FCSTD DOCUMENT  (FreeCAD 1.0R39109 (Git))
Label: bridge_S
License: All rights reserved
LicenseURL: https://en.wikipedia.org/wiki/All_rights_reserved
objects: Part::FeaturePython×26, Sketcher::SketchObject×11, Part::Extrusion×9, App::Part×5, Part::Sweep×4, Part::Compound×4, Part::MultiFuse×2, Spreadsheet::Sheet×1, Part::Mirroring×1, PartDesign::FeatureBase×1, PartDesign::Pocket×1, PartDesign::Body×1, Part::Feature×1, PartDesign::Pad×1
note: 74 computed .brp shape members not serialized (recipe doc carries the construction recipe); baked Part::Feature solids carry a one-line shape summary decoded from their .brp

FEATURE [Part::FeaturePython] HShapeSteel  # WARN: FeaturePython — macro-defined, semantics opaque (R4)
  B = 200
  H = 294
  L = 5500
  Placement = pos=(0,-500,0) rot=(0,0,1;1.5708rad)
  Solid = false
  g0 = 7.85
  mass = 0
  size = 3
  standard = SS_Medium
  t1 = 8
  t2 = 12
  type = 02_H_Shape
FEATURE [Spreadsheet::Sheet] Spreadsheet  label="Spreadsheet_bridge"
  cells = A2='tankDia; B2(dia)=13000; A3='bridgeLength; B3(L0)==dia + 600; A4='hight; B4(hight)=600
FEATURE [Part::Extrusion] Extrude
  Base = -> HShapeSteel
  Dir = (-1,-2e-16,0)
  DirMode = 2
  FaceMakerClass = Part::FaceMakerBullseye
  FaceMakerMode = 3
  LengthFwd = 13600
  LengthRev = 0
  Solid = false
  Symmetric = true
  expr: LengthFwd = Spreadsheet.L0
FEATURE [Part::FeaturePython] Clone  label="Extrude001"  # Draft clone (typed FeaturePython)
  AttacherType = Attacher::AttachEngine3D
  Fuse = false
  Objects = -> [Extrude]
  Placement = pos=(0,800,0) rot=(0,0,1;0rad)
  Scale = (1,1,1)
  expr: .Placement.Base.y = 1000 - HShapeSteel.B
FEATURE [Part::FeaturePython] ChannelSteel  # WARN: FeaturePython — macro-defined, semantics opaque (R4)
  B = 75
  H = 150
  L = 5500
  Placement = pos=(-1000,0,0) rot=(0,0,1;0rad)
  Solid = false
  g0 = 7.85
  mass = 0
  size = 3
  standard = SS
  t1 = 6.5
  t2 = 10
  type = 01_Channel
FEATURE [Sketcher::SketchObject] Sketch
  ArcFitTolerance = 1e-06
  FullyConstrained = true
  MakeInternals = false
  sketch-geometry (5):
    g0: LineSegment StartX=-1000 StartY=-1000 StartZ=0 EndX=1000 EndY=-1000 EndZ=0
    g1: LineSegment StartX=1000 StartY=-1000 StartZ=0 EndX=1000 EndY=1000 EndZ=0
    g2: LineSegment StartX=1000 StartY=1000 StartZ=0 EndX=-1000 EndY=1000 EndZ=0
    g3: LineSegment StartX=-1000 StartY=1000 StartZ=0 EndX=-1000 EndY=-1000 EndZ=0
    g4: GeomPoint [constr] X=0 Y=0 Z=0
  constraints (12):
    c: Coincident(g0,g1)
    c: Coincident(g1,g2)
    c: Coincident(g2,g3)
    c: Coincident(g3,g0)
    c: Horizontal(g0)
    c: Horizontal(g2)
    c: Vertical(g1)
    c: Vertical(g3)
    c: Symmetric(g2,g0,g4)
    c: Coincident(g4,g-1)
    c: DistanceX(g2,g2) = 2000
    c: DistanceY(g3,g3) = 2000
FEATURE [Part::Sweep] Sweep
  Frenet = true
  Placement = pos=(0,0,144) rot=(0,0,1;0rad)
  Sections = -> [ChannelSteel]
  Solid = true
  Spine = -> Sketch [Edge4,Edge3,Edge2,Edge1]
  Transition = 1
FEATURE [Part::FeaturePython] AngleSteel  # WARN: FeaturePython — macro-defined, semantics opaque (R4)
  A = 65
  B = 65
  L = 5500
  Placement = pos=(-6800,0,0) rot=(0,0,1;0rad)
  Solid = false
  g0 = 7.85
  mass = 0
  size = 8
  standard = SS_Equal
  t = 6
  type = 00_Angle
FEATURE [Part::FeaturePython] AngleSteel001  # WARN: FeaturePython — macro-defined, semantics opaque (R4)
  A = 65
  B = 65
  L = 5500
  Placement = pos=(-6800,0,294) rot=(0,1,0;1.5708rad)
  Solid = false
  g0 = 7.85
  mass = 0
  size = 8
  standard = SS_Equal
  t = 6
  type = 00_Angle
FEATURE [Part::Extrusion] Extrude001  label="Extrude002"
  Base = -> AngleSteel001
  Dir = (0,1,0)
  DirMode = 2
  FaceMakerClass = Part::FaceMakerBullseye
  FaceMakerMode = 3
  LengthFwd = 600
  LengthRev = 0
  Solid = false
  Symmetric = true
  expr: LengthFwd = 1000 - HShapeSteel.B * 2
FEATURE [Part::Extrusion] Extrude002  label="Extrude003"
  Base = -> AngleSteel
  Dir = (0,1,0)
  DirMode = 2
  FaceMakerClass = Part::FaceMakerBullseye
  FaceMakerMode = 3
  LengthFwd = 600
  LengthRev = 0
  Solid = false
  Symmetric = true
  expr: LengthFwd = 1000 - HShapeSteel.B * 2
FEATURE [Part::Compound] Compound
  Links = -> [Extrude001,Extrude002]
FEATURE [Part::FeaturePython] Array  # Draft array (typed FeaturePython)
  AlwaysSyncPlacement = false
  Angle = 360
  ArrayType = 0
  Axis = (0,0,1)
  Base = -> Compound
  Center = (0,0,0)
  Count = 3
  ExpandArray = false
  Fuse = false
  IntervalAxis = (0,0,0)
  IntervalX = (2000,0,0)
  IntervalY = (0,100,0)
  IntervalZ = (0,0,100)
  NumberCircles = 3
  NumberPolar = 5
  NumberX = 3
  NumberY = 1
  NumberZ = 1
  PlacementList = 3 placements: arithmetic series from (0,0,0) step (2000,0,0) to (4000,0,0)
  RadialDistance = 50
  ScaleList = (3) [(1,1,1),(1,1,1),(1,1,1)]
  Symmetry = 1
  TangentialDistance = 25
FEATURE [Part::Mirroring] Mirror  label="Array (mirrored)"
  Base = (0,2000,0)
  Normal = (1,0,0)
  Source = -> Array
FEATURE [Sketcher::SketchObject] Sketch001
  ArcFitTolerance = 1e-06
  AttachmentSupport = -> [Extrude]
  FullyConstrained = true
  MakeInternals = false
  MapMode = 5
  Placement = pos=(0,0,294) rot=(0,0,1;0rad)
  expr: Constraints[25] = Spreadsheet.dia + 600
  sketch-geometry (12):
    g0: LineSegment StartX=-6800 StartY=500 StartZ=0 EndX=-1000 EndY=500 EndZ=0
    g1: LineSegment StartX=-1000 StartY=500 StartZ=0 EndX=-1000 EndY=1000 EndZ=0
    g2: LineSegment StartX=-1000 StartY=1000 StartZ=0 EndX=1000 EndY=1000 EndZ=0
    g3: LineSegment StartX=1000 StartY=1000 StartZ=0 EndX=1000 EndY=500 EndZ=0
    g4: LineSegment StartX=1000 StartY=500 StartZ=0 EndX=6800 EndY=500 EndZ=0
    g5: LineSegment StartX=6800 StartY=500 StartZ=0 EndX=6800 EndY=-500 EndZ=0
    g6: LineSegment StartX=6800 StartY=-500 StartZ=0 EndX=1000 EndY=-500 EndZ=0
    g7: LineSegment StartX=1000 StartY=-500 StartZ=0 EndX=1000 EndY=-1000 EndZ=0
    g8: LineSegment StartX=1000 StartY=-1000 StartZ=0 EndX=-1000 EndY=-1000 EndZ=0
    g9: LineSegment StartX=-1000 StartY=-1000 StartZ=0 EndX=-1000 EndY=-500 EndZ=0
    g10: LineSegment StartX=-1000 StartY=-500 StartZ=0 EndX=-6800 EndY=-500 EndZ=0
    g11: LineSegment StartX=-6800 StartY=-500 StartZ=0 EndX=-6800 EndY=500 EndZ=0
  constraints (33):
    c: Horizontal(g0)
    c: Coincident(g0,g1)
    c: Vertical(g1)
    c: Coincident(g1,g2)
    c: Horizontal(g2)
    c: Coincident(g2,g3)
    c: Vertical(g3)
    c: Coincident(g3,g4)
    c: Horizontal(g4)
    c: Coincident(g4,g5)
    c: Vertical(g5)
    c: Coincident(g5,g6)
    c: Horizontal(g6)
    c: Coincident(g6,g7)
    c: Vertical(g7)
    c: Coincident(g7,g8)
    c: Coincident(g8,g9)
    c: Vertical(g9)
    c: Coincident(g9,g10)
    c: Horizontal(g10)
    c: Coincident(g10,g11)
    c: Coincident(g11,g0)
    c: Symmetric(g10,g0,g-1)
    c: DistanceY(g11,g11) = 1000
    c: Symmetric(g10,g5,g-2)
    c: DistanceX(g10,g5) = 13600
    c: Horizontal(g0,g3)
    c: Vertical(g0,g9)
    c: DistanceX(g8,g8) = 2000
    c: Symmetric(g8,g7,g-2)
    c: Vertical(g6,g3)
    c: DistanceY(g7,g2) = 2000
    c: Distance(g7,g-1) = 1000
FEATURE [Part::Extrusion] Extrude003  label="Extrude004"
  Base = -> Sketch001
  Dir = (0,0,1)
  DirMode = 2
  FaceMakerClass = Part::FaceMakerBullseye
  FaceMakerMode = 3
  LengthFwd = 4.5
  LengthRev = 0
  Solid = true
  Symmetric = false
FEATURE [Part::Compound] Compound001
  Links = -> [Mirror,Array]
FEATURE [Part::FeaturePython] ChannelSteel001  # WARN: FeaturePython — macro-defined, semantics opaque (R4)
  B = 75
  H = 150
  L = 5500
  Placement = pos=(250,0,0) rot=(0,0,1;0rad)
  Solid = false
  g0 = 7.85
  mass = 0
  size = 3
  standard = SS
  t1 = 6.5
  t2 = 10
  type = 01_Channel
FEATURE [Part::Extrusion] Extrude004  label="Extrude005"
  Base = -> ChannelSteel001
  Dir = (0,1,0)
  DirMode = 2
  FaceMakerClass = Part::FaceMakerBullseye
  FaceMakerMode = 3
  LengthFwd = 600
  LengthRev = 0
  Placement = pos=(0,0,144) rot=(0,0,1;0rad)
  Solid = false
  Symmetric = true
  expr: LengthFwd = 1000 - HShapeSteel.B * 2
FEATURE [Part::FeaturePython] Array001  # Draft array (typed FeaturePython)
  AlwaysSyncPlacement = false
  Angle = 360
  ArrayType = 1
  Axis = (0,0,1)
  Base = -> Extrude004
  Center = (0,0,0)
  Count = 2
  ExpandArray = false
  Fuse = false
  IntervalAxis = (0,0,0)
  IntervalX = (50,0,0)
  IntervalY = (0,50,0)
  IntervalZ = (0,0,50)
  NumberCircles = 3
  NumberPolar = 2
  NumberX = 2
  NumberY = 2
  NumberZ = 1
  PlacementList = 2 placements: [(0,0,144),(0,0,144)]
  RadialDistance = 50
  ScaleList = (2) [(1,1,1),(1,1,1)]
  Symmetry = 1
  TangentialDistance = 25
FEATURE [Sketcher::SketchObject] Sketch002
  ArcFitTolerance = 1e-06
  AttachmentSupport = -> [Extrude003]
  FullyConstrained = true
  MakeInternals = false
  MapMode = 5
  Placement = pos=(0,0,298.5) rot=(0,0,1;0rad)
  sketch-geometry (4):
    g0: LineSegment StartX=6800 StartY=500 StartZ=0 EndX=8110 EndY=500 EndZ=0
    g1: LineSegment StartX=8110 StartY=500 StartZ=0 EndX=8110 EndY=-500 EndZ=0
    g2: LineSegment StartX=8110 StartY=-500 StartZ=0 EndX=6800 EndY=-500 EndZ=0
    g3: LineSegment StartX=6800 StartY=-500 StartZ=0 EndX=6800 EndY=500 EndZ=0
  constraints (10):
    c: Horizontal(g0)
    c: Coincident(g0,g1)
    c: Vertical(g1)
    c: Coincident(g1,g2)
    c: Horizontal(g2)
    c: Coincident(g0,g-3)
    c: Coincident(g2,g-3)
    c: DistanceX(g2,g2) = 1310
    c: Coincident(g3,g2)
    c: Coincident(g3,g0)
FEATURE [Part::FeaturePython] ChannelSteel002  # WARN: FeaturePython — macro-defined, semantics opaque (R4)
  B = 75
  H = 150
  L = 5500
  Placement = pos=(8110,0,294) rot=(0,1,0;3.14159rad)
  Solid = false
  g0 = 7.85
  mass = 0
  size = 3
  standard = SS
  t1 = 6.5
  t2 = 10
  type = 01_Channel
FEATURE [Part::Sweep] Sweep001
  Frenet = true
  Sections = -> [ChannelSteel002]
  Solid = true
  Spine = -> Sketch002 [Edge3,Edge2,Edge1,Edge4]
  Transition = 1
FEATURE [Sketcher::SketchObject] Sketch003
  ArcFitTolerance = 1e-06
  AttachmentSupport = -> [Sweep001]
  ExternalGeometry = -> [Sweep001,Sketch002]
  FullyConstrained = true
  MakeInternals = false
  MapMode = 5
  Placement = pos=(0,3.6e-14,294) rot=(0,0,1;0rad)
  sketch-geometry (9):
    g0: LineSegment StartX=6850 StartY=-450 StartZ=0 EndX=8060 EndY=-450 EndZ=0
    g1: LineSegment StartX=8060 StartY=-450 StartZ=0 EndX=8060 EndY=450 EndZ=0
    g2: LineSegment StartX=8060 StartY=450 StartZ=0 EndX=6850 EndY=450 EndZ=0
    g3: LineSegment StartX=6850 StartY=450 StartZ=0 EndX=6850 EndY=-450 EndZ=0
    g4: GeomPoint [constr] X=7455 Y=2.715e-13 Z=0
    g5: LineSegment StartX=6800 StartY=-500 StartZ=0 EndX=8110 EndY=-500 EndZ=0
    g6: LineSegment StartX=8110 StartY=-500 StartZ=0 EndX=8110 EndY=500 EndZ=0
    g7: LineSegment StartX=8110 StartY=500 StartZ=0 EndX=6800 EndY=500 EndZ=0
    g8: LineSegment StartX=6800 StartY=500 StartZ=0 EndX=6800 EndY=-500 EndZ=0
  constraints (23):
    c: Coincident(g0,g1)
    c: Coincident(g1,g2)
    c: Coincident(g2,g3)
    c: Coincident(g3,g0)
    c: Horizontal(g0)
    c: Horizontal(g2)
    c: Vertical(g1)
    c: Vertical(g3)
    c: Symmetric(g2,g0,g4)
    c: DistanceY(g0,g-4) = 25
    c: Distance(g-4,g3) = 25
    c: DistanceY(g-3,g1) = 25
    c: DistanceX(g-3,g1) = 25
    c: Coincident(g5,g6)
    c: Coincident(g6,g7)
    c: Coincident(g7,g8)
    c: Coincident(g8,g5)
    c: Horizontal(g5)
    c: Horizontal(g7)
    c: Vertical(g6)
    c: Vertical(g8)
    c: Coincident(g-6,g6)
    c: Coincident(g-5,g5)
FEATURE [Part::Extrusion] Extrude005  label="Extrude006"
  Base = -> Sketch003
  Dir = (0,0,1)
  DirMode = 2
  FaceMakerClass = Part::FaceMakerBullseye
  FaceMakerMode = 3
  LengthFwd = 4.5
  LengthRev = 0
  Solid = true
  Symmetric = false
FEATURE [Sketcher::SketchObject] Sketch004
  ArcFitTolerance = 1e-06
  AttachmentSupport = -> [XY_Plane002]
  FullyConstrained = true
  MakeInternals = false
  MapMode = 5
  sketch-geometry (5):
    g0: LineSegment StartX=-302.5 StartY=-450 StartZ=0 EndX=302.5 EndY=-450 EndZ=0
    g1: LineSegment StartX=302.5 StartY=-450 StartZ=0 EndX=302.5 EndY=450 EndZ=0
    g2: LineSegment StartX=302.5 StartY=450 StartZ=0 EndX=-302.5 EndY=450 EndZ=0
    g3: LineSegment StartX=-302.5 StartY=450 StartZ=0 EndX=-302.5 EndY=-450 EndZ=0
    g4: GeomPoint [constr] X=0 Y=0 Z=0
  constraints (12):
    c: Coincident(g0,g1)
    c: Coincident(g1,g2)
    c: Coincident(g2,g3)
    c: Coincident(g3,g0)
    c: Horizontal(g0)
    c: Horizontal(g2)
    c: Vertical(g1)
    c: Vertical(g3)
    c: Symmetric(g2,g0,g4)
    c: Coincident(g4,g-1)
    c: DistanceY(g3,g3) = 900
    c: DistanceX(g2,g2) = 605
FEATURE [Sketcher::SketchObject] Sketch005
  ArcFitTolerance = 1e-06
  AttachmentSupport = -> [XY_Plane002]
  ExternalGeometry = -> [Sketch004]
  FullyConstrained = true
  MakeInternals = false
  MapMode = 5
  sketch-geometry (5):
    g0: LineSegment StartX=-272.5 StartY=-420 StartZ=0 EndX=272.5 EndY=-420 EndZ=0
    g1: LineSegment StartX=272.5 StartY=-420 StartZ=0 EndX=272.5 EndY=420 EndZ=0
    g2: LineSegment StartX=272.5 StartY=420 StartZ=0 EndX=-272.5 EndY=420 EndZ=0
    g3: LineSegment StartX=-272.5 StartY=420 StartZ=0 EndX=-272.5 EndY=-420 EndZ=0
    g4: GeomPoint [constr] X=0 Y=0 Z=0
  constraints (12):
    c: Coincident(g0,g1)
    c: Coincident(g1,g2)
    c: Coincident(g2,g3)
    c: Coincident(g3,g0)
    c: Horizontal(g0)
    c: Horizontal(g2)
    c: Vertical(g1)
    c: Vertical(g3)
    c: Symmetric(g2,g0,g4)
    c: Coincident(g4,g-1)
    c: DistanceX(g1,g-3) = 30
    c: DistanceY(g1,g-3) = 30
FEATURE [Part::FeaturePython] AngleSteel002  # WARN: FeaturePython — macro-defined, semantics opaque (R4)
  A = 50
  B = 50
  L = 5500
  Placement = pos=(275,0,3.74e-14) rot=(0,1,0;3.14159rad)
  Solid = false
  g0 = 7.85
  mass = 0
  size = 6
  standard = SS_Equal
  t = 4
  type = 00_Angle
FEATURE [Part::Extrusion] Extrude006  label="Extrude007"
  Base = -> Sketch004
  Dir = (0,0,1)
  DirMode = 2
  FaceMakerClass = Part::FaceMakerBullseye
  FaceMakerMode = 3
  LengthFwd = 4.5
  LengthRev = 0
  Solid = true
  Symmetric = false
FEATURE [Part::Sweep] Sweep002
  Frenet = true
  Sections = -> [AngleSteel002]
  Solid = true
  Spine = -> Sketch005 [Edge2,Edge3,Edge4,Edge1]
  Transition = 1
FEATURE [PartDesign::FeatureBase] BaseFeature
  BaseFeature = -> Extrude006
  Suppressed = false
FEATURE [Sketcher::SketchObject] Sketch006
  ArcFitTolerance = 1e-06
  AttachmentSupport = -> [BaseFeature]
  FullyConstrained = true
  MakeInternals = false
  MapMode = 5
  Placement = pos=(0,0,4.5) rot=(0,0,1;0rad)
  sketch-geometry (8):
    g0: LineSegment StartX=-48.25 StartY=225 StartZ=0 EndX=48.25 EndY=225 EndZ=0
    g1: LineSegment StartX=48.25 StartY=225 StartZ=0 EndX=48.25 EndY=265 EndZ=0
    g2: LineSegment StartX=48.25 StartY=265 StartZ=0 EndX=-48.25 EndY=265 EndZ=0
    g3: LineSegment StartX=-48.25 StartY=265 StartZ=0 EndX=-48.25 EndY=225 EndZ=0
    g4: LineSegment StartX=-48.25 StartY=-265 StartZ=0 EndX=48.25 EndY=-265 EndZ=0
    g5: LineSegment StartX=48.25 StartY=-265 StartZ=0 EndX=48.25 EndY=-225 EndZ=0
    g6: LineSegment StartX=48.25 StartY=-225 StartZ=0 EndX=-48.25 EndY=-225 EndZ=0
    g7: LineSegment StartX=-48.25 StartY=-225 StartZ=0 EndX=-48.25 EndY=-265 EndZ=0
  constraints (23):
    c: Coincident(g0,g1)
    c: Coincident(g1,g2)
    c: Coincident(g2,g3)
    c: Coincident(g3,g0)
    c: Horizontal(g2)
    c: Vertical(g1)
    c: Vertical(g3)
    c: Coincident(g4,g5)
    c: Coincident(g5,g6)
    c: Coincident(g6,g7)
    c: Coincident(g7,g4)
    c: Horizontal(g4)
    c: Horizontal(g6)
    c: Vertical(g5)
    c: Vertical(g7)
    c: DistanceX(g2,g2) = 96.5
    c: DistanceY(g1,g1) = 40
    c: Vertical(g0,g6)
    c: Vertical(g0,g5)
    c: Symmetric(g0,g0,g-2)
    c: DistanceY(g-1,g0) = 225
    c: DistanceY(g5,g5) = 40
    c: DistanceY(g5,g-1) = 225
FEATURE [PartDesign::Pocket] Pocket
  BaseFeature = -> BaseFeature
  Direction = (0,0,-1)
  Length = 5
  Length2 = 5
  Profile = -> Sketch006
  ReferenceAxis = -> Sketch006 [N_Axis]
  Suppressed = false
  Type = 0
FEATURE [PartDesign::Body] Body
  AllowCompound = false
  BaseFeature = -> Extrude006
  Group = -> [BaseFeature,Sketch006,Pocket]
  Origin = -> Origin002
  Tip = -> Pocket
FEATURE [Part::Feature] Part__Feature001  label="AP-268-2\X\96{\X\91\X\CC__\X\C3\X\DE\X\CC\X\AB\X\D9\X\\\\C005"
  Placement = pos=(1044.74,-585.443,742.289) rot=(0,0,1;0rad)
  shape: bbox 104.7 x 52.9 x 35.45 mm, 341 faces (baked)
FEATURE [App::Part] AP_268_2_black_v004  label="AP-268-2-black v004"
  Group = -> [Part__Feature001]
  Origin = -> Origin004
  Placement = pos=(-154,-42.5,-734) rot=(0,0,1;0rad)
FEATURE [Part::FeaturePython] Array002  # Draft array (typed FeaturePython)
  AlwaysSyncPlacement = false
  Angle = 360
  ArrayType = 1
  Axis = (0,0,1)
  Base = -> AP_268_2_black_v004
  Center = (0,0,0)
  Count = 2
  ExpandArray = false
  Fuse = false
  IntervalAxis = (0,0,0)
  IntervalX = (50,0,0)
  IntervalY = (0,50,0)
  IntervalZ = (0,0,50)
  NumberCircles = 3
  NumberPolar = 2
  NumberX = 2
  NumberY = 2
  NumberZ = 1
  PlacementList = 2 placements: [(-154,-42.5,-734),(154,42.5,-734)]
  RadialDistance = 50
  ScaleList = (2) [(1,1,1),(1,1,1)]
  Symmetry = 1
  TangentialDistance = 25
FEATURE [Part::FeaturePython] Channel  # WARN: FeaturePython — macro-defined, semantics opaque (R4)
  Placement = pos=(0,-975,298.5) rot=(0,0,1;0rad)
  Reverse = false
  g0 = 7.85
  h = 1100
  k = 90
  l1 = 975
  l2 = 249
  mass = 28.2367
  p = 500
  spec = 0
  type = 6
FEATURE [Part::FeaturePython] Corner_with_end001  # WARN: FeaturePython — macro-defined, semantics opaque (R4)
  Placement = pos=(-6735.5,-474.5,299) rot=(0,0,1;0rad)
  Reverse = false
  g0 = 7.85
  h = 1100
  k = -90
  l1 = 5760
  l2 = 249
  mass = 85.141
  p = 500
  spec = 0
  type = 1
  expr: .Placement.Base.x = -6735.5 - (Spreadsheet.dia - 13000) / 2
  expr: l1 = 5760 + (Spreadsheet.dia - 13000) / 2
FEATURE [Part::Compound] Compound003
  Links = -> [Sweep002,Extrude006,Body,Array002]
  expr: .Placement.Base.x = (Spreadsheet.dia - 13000) / 2
FEATURE [App::Part] Part002  label="inspectionCover"
  Group = -> [Sketch004,Sketch005,Sweep002,AngleSteel002,Extrude006,Body,AP_268_2_black_v004,Array002,Compound003]
  Origin = -> Origin003
  Placement = pos=(7758,0,294) rot=(0,0,1;0rad)
FEATURE [Part::FeaturePython] Clone001  label="inspectionCover001"  # Draft clone (typed FeaturePython)
  AttacherType = Attacher::AttachEngine3D
  Fuse = false
  Objects = -> [Part002]
  Placement = pos=(7153,0,294) rot=(0,0,1;0rad)
  Scale = (1,1,1)
FEATURE [Part::FeaturePython] Corner_with_end002  # WARN: FeaturePython — macro-defined, semantics opaque (R4)
  Placement = pos=(-6735.5,469.5,299) rot=(0,0,1;0rad)
  Reverse = true
  g0 = 7.85
  h = 1100
  k = 90
  l1 = 5760
  l2 = 249
  mass = 85.141
  p = 500
  spec = 0
  type = 1
  expr: .Placement.Base.x = -6735.5 - (Spreadsheet.dia - 13000) / 2
  expr: l1 = 5760 + (Spreadsheet.dia - 13000) / 2
FEATURE [Part::FeaturePython] Channel001  # WARN: FeaturePython — macro-defined, semantics opaque (R4)
  Placement = pos=(0,-975,298.5) rot=(0,0,1;0rad)
  Reverse = false
  g0 = 7.85
  h = 1100
  k = 90
  l1 = 975
  l2 = 249
  mass = 28.2367
  p = 500
  spec = 0
  type = 6
FEATURE [Part::FeaturePython] Channel002  # WARN: FeaturePython — macro-defined, semantics opaque (R4)
  Placement = pos=(0,973.5,298.5) rot=(0,0,1;0rad)
  Reverse = true
  g0 = 7.85
  h = 1100
  k = -90
  l1 = 975
  l2 = 249
  mass = 28.2367
  p = 500
  spec = 0
  type = 6
FEATURE [Part::FeaturePython] Corner  # WARN: FeaturePython — macro-defined, semantics opaque (R4)
  Placement = pos=(6976,474,298) rot=(0,0,1;3.14159rad)
  Reverse = false
  g0 = 7.85
  h = 1100
  k = -90
  l1 = 6000
  l2 = 240
  mass = 85.8466
  p = 500
  spec = 0
  type = 2
  expr: .Placement.Base.x = 6976 + (Spreadsheet.dia - 13000) / 2
  expr: l1 = 6000 + (Spreadsheet.dia - 13000) / 2
FEATURE [Part::FeaturePython] Corner_with_end003  # WARN: FeaturePython — macro-defined, semantics opaque (R4)
  Placement = pos=(8085,-434.5,299) rot=(0,0,1;1.5708rad)
  Reverse = false
  g0 = 7.85
  h = 1100
  k = 90
  l1 = 910
  l2 = 1102
  mass = 26.1239
  p = 1000
  spec = 0
  type = 1
  expr: .Placement.Base.x = 8085 + (Spreadsheet.dia - 13000) / 2
FEATURE [Part::FeaturePython] SquarePipe  # WARN: FeaturePython — macro-defined, semantics opaque (R4)
  A = 200
  B = 200
  L = 306
  Placement = pos=(0,0,-300) rot=(0,0,1;0rad)
  Solid = true
  g0 = 7.85
  mass = 10.9615
  size = 44
  standard = SS
  t = 4.5
  type = 10_Square_Pipe
  expr: .Placement.Base.z = -(Spreadsheet.hight - 294) + 6
  expr: L = <<Spreadsheet_bridge>>.hight - 294
FEATURE [Sketcher::SketchObject] Sketch007
  ArcFitTolerance = 1e-06
  AttachmentSupport = -> [SquarePipe]
  ExternalGeometry = -> [SquarePipe]
  FullyConstrained = true
  MakeInternals = false
  MapMode = 5
  Placement = pos=(0,0,-300) rot=(1,0,0;3.14159rad)
  sketch-geometry (9):
    g0: LineSegment StartX=-138 StartY=-150 StartZ=0 EndX=138 EndY=-150 EndZ=0
    g1: LineSegment StartX=138 StartY=-150 StartZ=0 EndX=138 EndY=150 EndZ=0
    g2: LineSegment StartX=138 StartY=150 StartZ=0 EndX=-138 EndY=150 EndZ=0
    g3: LineSegment StartX=-138 StartY=150 StartZ=0 EndX=-138 EndY=-150 EndZ=0
    g4: GeomPoint [constr] X=-2e-16 Y=3e-16 Z=0
    g5: Circle CenterX=-113 CenterY=125 CenterZ=0 NormalX=0 NormalY=0 NormalZ=1 AngleXU=0 Radius=10
    g6: Circle CenterX=-113 CenterY=-125 CenterZ=0 NormalX=0 NormalY=0 NormalZ=1 AngleXU=0 Radius=10
    g7: Circle CenterX=113 CenterY=-125 CenterZ=0 NormalX=0 NormalY=0 NormalZ=1 AngleXU=0 Radius=10
    g8: Circle CenterX=113 CenterY=125 CenterZ=0 NormalX=0 NormalY=0 NormalZ=1 AngleXU=0 Radius=10
  constraints (24):
    c: Coincident(g0,g1)
    c: Coincident(g1,g2)
    c: Coincident(g2,g3)
    c: Coincident(g3,g0)
    c: Horizontal(g0)
    c: Horizontal(g2)
    c: Vertical(g1)
    c: Vertical(g3)
    c: Symmetric(g2,g0,g4)
    c: Coincident(g4,g-1)
    c: DistanceY(g-3,g1) = 50
    c: DistanceX(g-5,g0) = 50
    c: Diameter(g5) = 20
    c: Equal(g5,g6)
    c: Equal(g6,g7)
    c: Equal(g7,g8)
    c: Vertical(g5,g6)
    c: Vertical(g8,g7)
    c: Horizontal(g5,g8)
    c: Horizontal(g6,g7)
    c: DistanceY(g5,g2) = 25
    c: DistanceX(g2,g5) = 25
    c: DistanceX(g8,g1) = 25
    c: DistanceY(g0,g7) = 25
FEATURE [PartDesign::Pad] Pad  label="plt"
  Direction = (0,0,-1)
  Length = 9
  Length2 = 10
  Placement = pos=(0,0,-300) rot=(0,0,1;0rad)
  Profile = -> Sketch007
  ReferenceAxis = -> Sketch007 [N_Axis]
  Refine = true
  Reversed = true
  Suppressed = false
  Type = 0
FEATURE [Sketcher::SketchObject] Sketch008
  ArcFitTolerance = 1e-06
  AttachmentSupport = -> [SquarePipe]
  ExternalGeometry = -> [SquarePipe]
  FullyConstrained = true
  MakeInternals = false
  MapMode = 5
  Placement = pos=(0,3.4e-14,6) rot=(0,0,1;0rad)
  sketch-geometry (13):
    g0: LineSegment StartX=-88 StartY=-100 StartZ=0 EndX=88 EndY=-100 EndZ=0
    g1: LineSegment StartX=100 StartY=-88 StartZ=0 EndX=100 EndY=88 EndZ=0
    g2: LineSegment StartX=88 StartY=100 StartZ=0 EndX=-88 EndY=100 EndZ=0
    g3: LineSegment StartX=-100 StartY=88 StartZ=0 EndX=-100 EndY=-88 EndZ=0
    g4: GeomPoint [constr] X=0 Y=0 Z=0
    g5: ArcOfCircle CenterX=88 CenterY=88 CenterZ=0 NormalX=0 NormalY=0 NormalZ=1 AngleXU=0 Radius=12 StartAngle=1e-16 EndAngle=1.5708
    g6: GeomPoint [constr] X=100 Y=100 Z=0
    g7: ArcOfCircle CenterX=-88 CenterY=88 CenterZ=0 NormalX=0 NormalY=0 NormalZ=1 AngleXU=0 Radius=12 StartAngle=1.5708 EndAngle=3.14159
    g8: GeomPoint [constr] X=-100 Y=100 Z=0
    g9: ArcOfCircle CenterX=-88 CenterY=-88 CenterZ=0 NormalX=0 NormalY=0 NormalZ=1 AngleXU=0 Radius=12 StartAngle=3.14159 EndAngle=4.71239
    g10: GeomPoint [constr] X=-100 Y=-100 Z=0
    g11: ArcOfCircle CenterX=88 CenterY=-88 CenterZ=0 NormalX=0 NormalY=0 NormalZ=1 AngleXU=0 Radius=12 StartAngle=4.71239 EndAngle=6.28319
    g12: GeomPoint [constr] X=100 Y=-100 Z=0
  constraints (28):
    c: Horizontal(g0)
    c: Horizontal(g2)
    c: Vertical(g1)
    c: Vertical(g3)
    c: Symmetric(g6,g10,g4)
    c: Coincident(g4,g-1)
    c: PointOnObject(g-4,g2)
    c: PointOnObject(g-3,g1)
    c: PointOnObject(g6,g2)
    c: PointOnObject(g6,g1)
    c: Tangent(g2,g5) = -1.5708
    c: Tangent(g1,g5) = -1.5708
    c: PointOnObject(g8,g2)
    c: PointOnObject(g8,g3)
    c: Tangent(g2,g7) = -1.5708
    c: Tangent(g3,g7) = -1.5708
    c: PointOnObject(g10,g0)
    c: PointOnObject(g10,g3)
    c: Tangent(g0,g9) = -1.5708
    c: Tangent(g3,g9) = -1.5708
    c: Equal(g5,g-5)
    c: PointOnObject(g12,g1)
    c: PointOnObject(g12,g0)
    c: Tangent(g1,g11) = -1.5708
    c: Tangent(g0,g11) = -1.5708
    c: Equal(g5,g7)
    c: Equal(g7,g9)
    c: Equal(g9,g11)
FEATURE [Part::Extrusion] Extrude007  label="Extrude008"
  Base = -> Sketch008
  Dir = (0,0,1)
  DirMode = 2
  FaceMakerClass = Part::FaceMakerBullseye
  FaceMakerMode = 3
  LengthFwd = 9
  LengthRev = 0
  Reversed = true
  Solid = true
  Symmetric = false
FEATURE [Part::MultiFuse] Fusion  label="Pst_SQ"
  Refine = true
  Shapes = -> [SquarePipe,Pad,Extrude007]
FEATURE [App::Part] Part004  label="pst_SQ"
  Group = -> [Sketch008,SquarePipe,Sketch007,Pad,Extrude007,Fusion]
  Origin = -> Origin006
  Placement = pos=(-6700,-400,0) rot=(0,0,1;0rad)
  expr: .Placement.Base.x = -Spreadsheet.L0 / 2 + 100
  expr: .Placement.Base.y = -400
FEATURE [Part::FeaturePython] Array003  # Draft array (typed FeaturePython)
  AlwaysSyncPlacement = false
  Angle = 360
  ArrayType = 0
  Axis = (0,0,1)
  Base = -> Part004
  Center = (0,0,0)
  Count = 4
  ExpandArray = false
  Fuse = false
  IntervalAxis = (0,0,0)
  IntervalX = (13400,0,0)
  IntervalY = (0,800,0)
  IntervalZ = (0,0,100)
  NumberCircles = 3
  NumberPolar = 5
  NumberX = 2
  NumberY = 2
  NumberZ = 1
  Placement = pos=(0,0,-6) rot=(0,0,1;0rad)
  PlacementList = 4 placements: [(-6700,-400,0),(-6700,400,0),(6700,-400,0),(6700,400,0)]
  RadialDistance = 50
  ScaleList = (4) [(1,1,1),(1,1,1),(1,1,1),(1,1,1)]
  Symmetry = 1
  TangentialDistance = 25
  expr: .IntervalX.x = Spreadsheet.L0 - 200
FEATURE [Part::Compound] Compound004
  Links = -> [Sweep001,Extrude005]
  expr: .Placement.Base.x = (Spreadsheet.dia - 13000) / 2
FEATURE [Sketcher::SketchObject] Sketch010
  ArcFitTolerance = 1e-06
  AttachmentSupport = -> [Extrude]
  FullyConstrained = true
  MakeInternals = false
  MapMode = 5
  Placement = pos=(0,0,294) rot=(0,0,1;0rad)
  expr: Constraints[9] = Spreadsheet.L0 / 2
  sketch-geometry (3):
    g0: LineSegment StartX=6800 StartY=-400 StartZ=0 EndX=6800 EndY=-900 EndZ=0
    g1: LineSegment StartX=6800 StartY=-900 StartZ=0 EndX=5300 EndY=-900 EndZ=0
    g2: LineSegment StartX=5300 StartY=-900 StartZ=0 EndX=5300 EndY=-400 EndZ=0
  constraints (10):
    c: Coincident(g0,g1)
    c: Horizontal(g1)
    c: Coincident(g1,g2)
    c: Vertical(g2)
    c: Vertical(g0)
    c: Horizontal(g2,g0)
    c: DistanceX(g1,g1) = 1500
    c: DistanceY(g1,g-1) = 900
    c: DistanceY(g2,g2) = 500
    c: DistanceX(g-1,g0) = 6800
FEATURE [Part::FeaturePython] ChannelSteel003  # WARN: FeaturePython — macro-defined, semantics opaque (R4)
  B = 75
  H = 150
  L = 5500
  Placement = pos=(5300,-800,140) rot=(0,0,1;0rad)
  Solid = false
  g0 = 7.85
  mass = 0
  size = 3
  standard = SS
  t1 = 6.5
  t2 = 10
  type = 01_Channel
  expr: .Placement.Base.x = Spreadsheet.dia / 2 - 1200
FEATURE [Sketcher::SketchObject] Sketch011
  ArcFitTolerance = 1e-06
  FullyConstrained = true
  MakeInternals = false
  MapMode = 5
  Placement = pos=(0,3.55e-14,290) rot=(0,0,1;0rad)
  expr: Constraints[10] = Spreadsheet.L0 / 2
  sketch-geometry (4):
    g0: LineSegment StartX=5300 StartY=-900 StartZ=0 EndX=6800 EndY=-900 EndZ=0
    g1: LineSegment StartX=6800 StartY=-500 StartZ=0 EndX=5300 EndY=-500 EndZ=0
    g2: LineSegment StartX=5300 StartY=-500 StartZ=0 EndX=5300 EndY=-900 EndZ=0
    g3: LineSegment StartX=6800 StartY=-500 StartZ=0 EndX=6800 EndY=-900 EndZ=0
  constraints (12):
    c: Coincident(g1,g2)
    c: Coincident(g2,g0)
    c: Horizontal(g0)
    c: DistanceX(g0,g0) = 1500
    c: Distance(g0,g-1) = 900
    c: Coincident(g3,g1)
    c: Coincident(g3,g0)
    c: Vertical(g3)
    c: Vertical(g2)
    c: Horizontal(g1)
    c: DistanceX(g-1,g0) = 6800
    c: DistanceY(g0,g1) = 400
FEATURE [Part::FeaturePython] Channel003  # WARN: FeaturePython — macro-defined, semantics opaque (R4)
  Placement = pos=(6050,-874.78,298) rot=(0,0,1;0rad)
  Reverse = false
  g0 = 7.85
  h = 1100
  k = 90
  l1 = 725
  l2 = 249
  mass = 24.1522
  p = 500
  spec = 0
  type = 6
  expr: .Placement.Base.x = Spreadsheet.L0 / 2 - 750
FEATURE [Part::FeaturePython] Corner001  # WARN: FeaturePython — macro-defined, semantics opaque (R4)
  Placement = pos=(3125.34,-469.24,299) rot=(0,0,1;0rad)
  Reverse = false
  g0 = 7.85
  h = 1100
  k = -90
  l1 = 2200
  l2 = 150
  mass = 30.7473
  p = 500
  spec = 0
  type = 2
  expr: l1 = 2200 + (Spreadsheet.dia - 13000) / 2
FEATURE [Part::FeaturePython] Corner002  # WARN: FeaturePython — macro-defined, semantics opaque (R4)
  Placement = pos=(3123.18,-468.54,298) rot=(0,0,1;3.14159rad)
  Reverse = true
  g0 = 7.85
  h = 1100
  k = 90
  l1 = 2150
  l2 = 249
  mass = 31.1476
  p = 500
  spec = 0
  type = 2
FEATURE [Part::FeaturePython] Edge_R  # WARN: FeaturePython — macro-defined, semantics opaque (R4)
  Placement = pos=(6775,-565.122,298.5) rot=(0,0,1;1.5708rad)
  Reverse = true
  g0 = 7.85
  h = 1100
  mass = 4.30234
  p = 500
  spec = 0
  type = 4
  expr: .Placement.Base.x = Spreadsheet.L0 / 2 - 25
FEATURE [App::Part] Part003  label="handrail"
  Group = -> [Channel,Corner_with_end001,Corner_with_end002,Channel001,Channel002,Corner,Corner_with_end003,Array003,Channel003,Corner001,Corner002,Edge_R]
  Origin = -> Origin005
FEATURE [Part::Sweep] Sweep003
  Frenet = true
  Sections = -> [ChannelSteel003]
  Solid = true
  Spine = -> Sketch010 [Edge3,Edge2,Edge1]
  Transition = 1
FEATURE [Part::Extrusion] Extrude008  label="Extrude009"
  Base = -> Sketch011
  Dir = (0,0,1)
  DirMode = 2
  FaceMakerClass = Part::FaceMakerBullseye
  FaceMakerMode = 3
  LengthFwd = 4.5
  LengthRev = 0
  Solid = true
  Symmetric = false
FEATURE [Part::MultiFuse] Fusion001
  Shapes = -> [Extrude003,Extrude,Compound001,Sweep,Clone,Array001,Extrude008,Sweep003]
FEATURE [App::Part] Part001  label="bridge_s"
  Group = -> [Spreadsheet,AngleSteel,AngleSteel001,Extrude001,Extrude002,Compound,ChannelSteel001,Extrude004,Sketch002,ChannelSteel002,Sweep001,Sketch003,Extrude005,Part002,Clone001,Part003,Compound004,Extrude003,Extrude,Sweep,Array,HShapeSteel,Clone,ChannelSteel,Array001,Sketch001,Compound001,Sketch,Mirror,Fusion001]
  Origin = -> Origin001
  Placement = pos=(0,0,5686) rot=(0,0,1;0rad)
